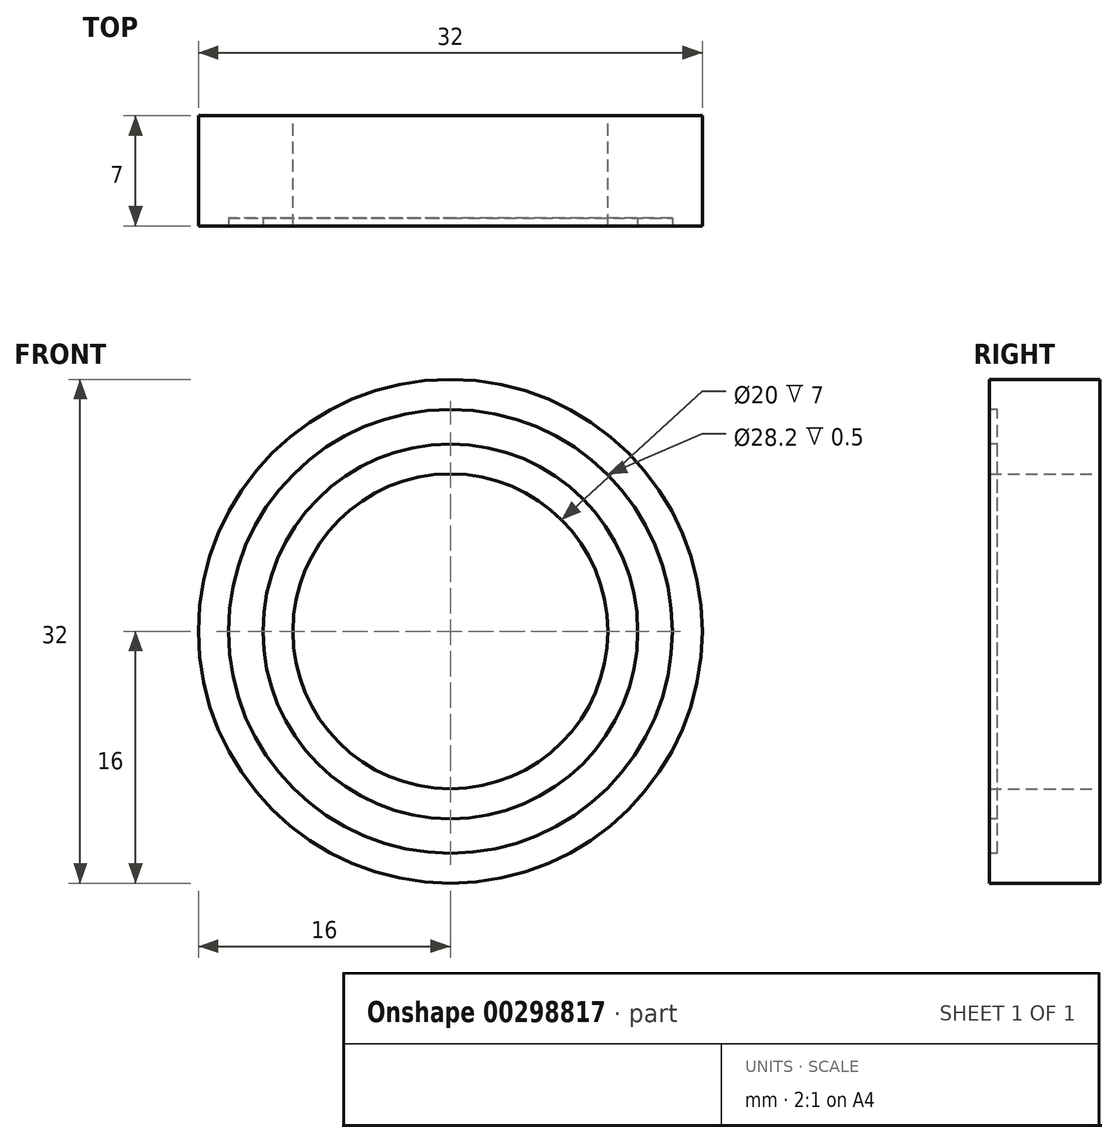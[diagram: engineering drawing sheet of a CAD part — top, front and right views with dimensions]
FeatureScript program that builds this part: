
annotation { "Feature Type Name" : "Feature", "Feature Type Description" : "" }
export const myFeature = defineFeature(function(context is Context, id is Id, definition is map)
    precondition{}
    {
        {
            var Q0;
            Q0=qCreatedBy(makeId("Front.planeOp"),FACE);
            var sketch = newSketch(context, id + "F0", { "sketchPlane" : qUnion([Q0])});
            skCircle(sketch, "E0", {"center": v(0, 0) * mm, "radius": 10 * mm});
            skCircle(sketch, "E1", {"center": v(0, 0) * mm, "radius": 16 * mm});
            skSolve(sketch);
        }
        {
            var Q0;
            Q0=makeQuery(id+"F0.imprint","IMPRINT",FACE,{"disambiguationData":[TD([[makeQuery(id+"F0.imprint","IMPRINT",EDGE,{"derivedFrom":sQuery(id+"F0.wireOp",EDGE,"E0")}),-1.0]])]});
            extrude(context, id + "F1", {"entities" : qUnion([Q0]), "depth" : 3.5 * mm, "hasSecondDirection" : true, "secondDirectionOppositeDirection" : true, "secondDirectionDepth" : 3.5 * mm});
        }
        {
            var Q0;
            Q0=makeQuery(id+"F1.opExtrude","CAP_FACE",FACE,{"disambiguationData":[OSD([sQuery(id+"F0.wireOp",EDGE,"E0"),sQuery(id+"F0.wireOp",EDGE,"E1")])],"isStart":false});
            var sketch = newSketch(context, id + "F2", { "sketchPlane" : qUnion([Q0])});
            skCircle(sketch, "E2", {"center": v(0, 0) * mm, "radius": 11.9 * mm});
            skCircle(sketch, "E3", {"center": v(0, 0) * mm, "radius": 14.1 * mm});
            skSolve(sketch);
        }
        {
            var Q0;
            Q0=makeQuery(id+"F2.imprint","IMPRINT",FACE,{"disambiguationData":[TD([[makeQuery(id+"F2.imprint","IMPRINT",EDGE,{"derivedFrom":sQuery(id+"F2.wireOp",EDGE,"E2")}),-1.0]])]});
            extrude(context, id + "F3", {"entities" : qUnion([Q0]), "operationType" : NewBodyOperationType.REMOVE, "oppositeDirection" : true, "depth" : 0.5 * mm});
        }
    });
